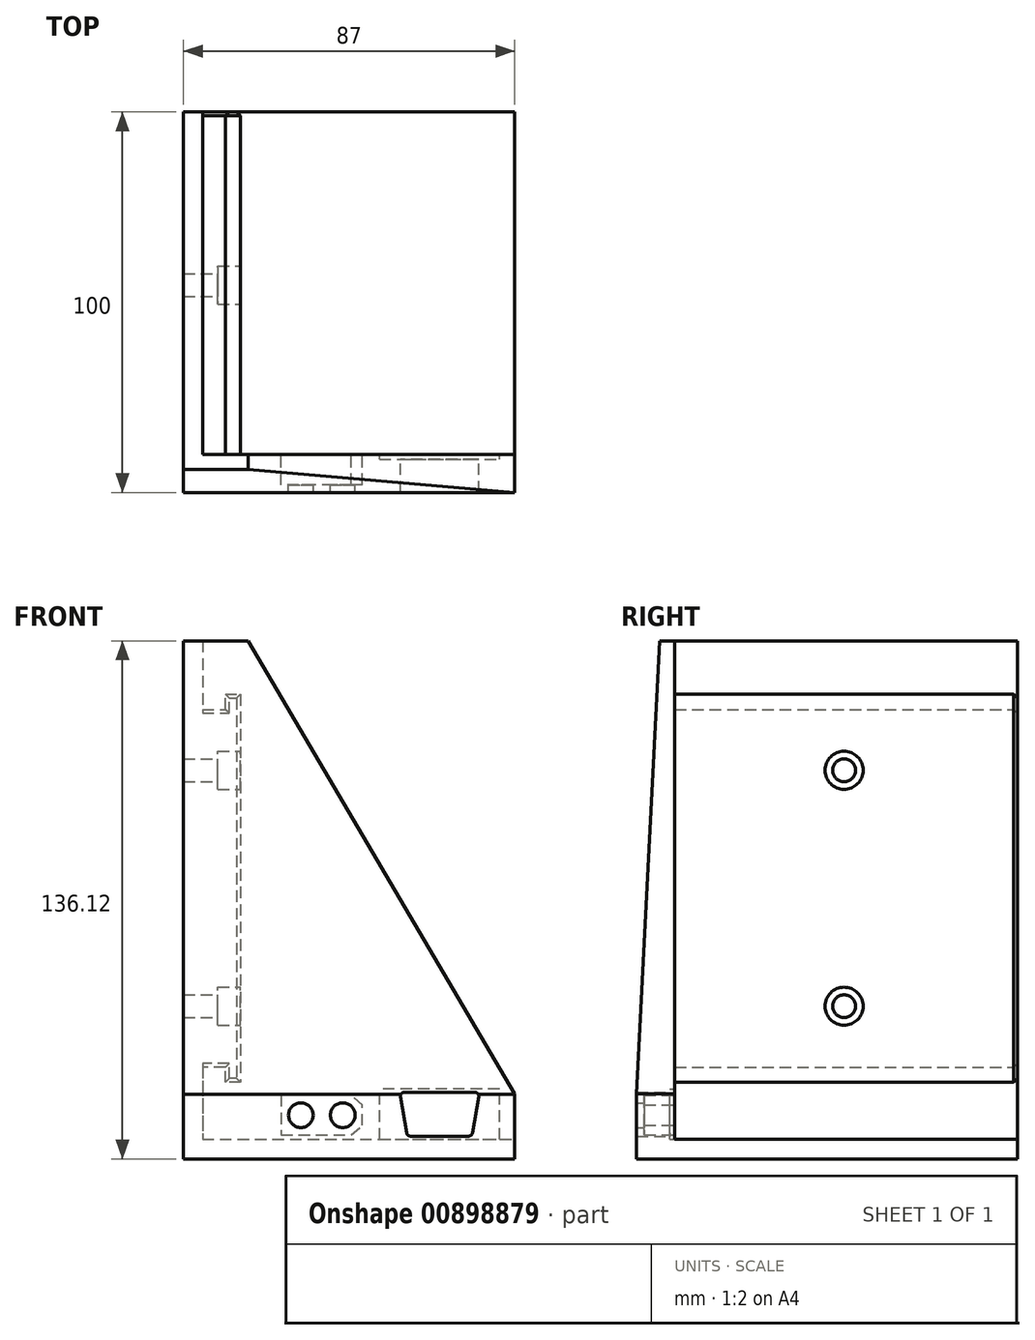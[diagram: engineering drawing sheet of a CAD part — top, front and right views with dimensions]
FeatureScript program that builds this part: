
annotation { "Feature Type Name" : "Feature", "Feature Type Description" : "" }
export const myFeature = defineFeature(function(context is Context, id is Id, definition is map)
    precondition{}
    {
        {
            var Q0;
            Q0=qCreatedBy(makeId("Front.planeOp"),FACE);
            var sketch = newSketch(context, id + "F0", { "sketchPlane" : qUnion([Q0])});
            skLineSegment(sketch, "E0", {"start": v(0, 131) * mm, "end": v(0, 0) * mm});
            skLineSegment(sketch, "E1", {"start": v(0, 131) * mm, "end": v(5, 131) * mm});
            skLineSegment(sketch, "E2", {"start": v(5, 131) * mm, "end": v(5, 113) * mm});
            skLineSegment(sketch, "E3", {"start": v(5, 113) * mm, "end": v(11, 113) * mm});
            skLineSegment(sketch, "E4", {"start": v(11, 113) * mm, "end": v(11, 117) * mm});
            skLineSegment(sketch, "E5", {"start": v(11, 117) * mm, "end": v(15, 117) * mm});
            skLineSegment(sketch, "E6", {"start": v(15, 117) * mm, "end": v(15, 15) * mm});
            skLineSegment(sketch, "E7", {"start": v(15, 15) * mm, "end": v(11, 15) * mm});
            skLineSegment(sketch, "E8", {"start": v(11, 15) * mm, "end": v(11, 19) * mm});
            skLineSegment(sketch, "E9", {"start": v(11, 19) * mm, "end": v(5, 19) * mm});
            skLineSegment(sketch, "E10", {"start": v(5, 19) * mm, "end": v(5, 0) * mm});
            skLineSegment(sketch, "E11", {"start": v(5, 0) * mm, "end": v(0, 0) * mm});
            skLineSegment(sketch, "E12", {"start": v(5, 0) * mm, "end": v(87, 0) * mm});
            skLineSegment(sketch, "E13", {"start": v(87, 0) * mm, "end": v(87, -5.12) * mm});
            skLineSegment(sketch, "E14", {"start": v(87, -5.12) * mm, "end": v(0, -5.12) * mm});
            skLineSegment(sketch, "E15", {"start": v(0, -5.12) * mm, "end": v(0, 0) * mm});
            skSolve(sketch);
        }
        {
            var Q0;
            Q0=qSketchRegion(id+"F0",true);
            extrude(context, id + "F1", {"entities" : qUnion([Q0]), "depth" : 90 * mm, "offsetDistance" : 25 * mm});
        }
        {
            var Q0;
            Q0=makeQuery(id+"F1.opExtrude","CAP_FACE",FACE,{"disambiguationData":[OSD([sQuery(id+"F0.wireOp",EDGE,"E0"),sQuery(id+"F0.wireOp",EDGE,"E1"),sQuery(id+"F0.wireOp",EDGE,"E2"),sQuery(id+"F0.wireOp",EDGE,"E3"),sQuery(id+"F0.wireOp",EDGE,"E4"),sQuery(id+"F0.wireOp",EDGE,"E5"),sQuery(id+"F0.wireOp",EDGE,"E6"),sQuery(id+"F0.wireOp",EDGE,"E7"),sQuery(id+"F0.wireOp",EDGE,"E8"),sQuery(id+"F0.wireOp",EDGE,"E9"),sQuery(id+"F0.wireOp",EDGE,"E10"),sQuery(id+"F0.wireOp",EDGE,"E12"),sQuery(id+"F0.wireOp",EDGE,"E13"),sQuery(id+"F0.wireOp",EDGE,"E14"),sQuery(id+"F0.wireOp",EDGE,"E15")])],"isStart":false});
            var sketch = newSketch(context, id + "F2", { "sketchPlane" : qUnion([Q0])});
            skLineSegment(sketch, "E16", {"start": v(87, 0) * mm, "end": v(87, 12) * mm});
            skLineSegment(sketch, "E17", {"start": v(87, 12) * mm, "end": v(17, 131) * mm});
            skLineSegment(sketch, "E18", {"start": v(17, 131) * mm, "end": v(5, 131) * mm});
            skSolve(sketch);
        }
        {
            var Q0;
            Q0=makeQuery(id+"F2.imprint","IMPRINT",FACE,{"disambiguationData":[TD([[makeQuery(id+"F2.imprint","IMPRINT",EDGE,{"derivedFrom":makeQuery(id+"F1.opExtrude","CAP_EDGE",EDGE,{"disambiguationData":[OSD([sQuery(id+"F0.wireOp",EDGE,"E1")])],"isStart":false})}),-1.0]])]});
            var Q1;
            Q1=makeQuery(id+"F2.imprint","IMPRINT",FACE,{"disambiguationData":[TD([[makeQuery(id+"F2.imprint","IMPRINT",EDGE,{"derivedFrom":sQuery(id+"F2.wireOp",EDGE,"E16")}),1.0]])]});
            extrude(context, id + "F3", {"entities" : qUnion([Q0, Q1]), "operationType" : NewBodyOperationType.ADD, "depth" : 10 * mm, "offsetDistance" : 25 * mm});
        }
        {
            var Q0;
            {var subQ0=sQuery(id+"F0.wireOp",EDGE,"E15");var subQ1=sQuery(id+"F0.wireOp",EDGE,"E0");Q0=makeQuery(id+"F3.boolean.opBoolean","MERGE",FACE,{"derivedFrom":[makeQuery(id+"F1.opExtrude","SWEPT_FACE",FACE,{"disambiguationData":[OSD([subQ1,subQ0])]}),makeQuery(id+"F3.opExtrude","SWEPT_FACE",FACE,{"disambiguationData":[OSD([subQ1,subQ0])]})]});}
            var sketch = newSketch(context, id + "F4", { "sketchPlane" : qUnion([Q0])});
            skLineSegment(sketch, "E19", {"start": v(94, 131) * mm, "end": v(100, 11.88) * mm});
            skSolve(sketch);
        }
        {
            var Q0;
            {var subQ0=sQuery(id+"F4.wireOp",EDGE,"E19");Q0=makeQuery(id+"F4.imprint","IMPRINT",FACE,{"disambiguationData":[TD([[makeQuery(id+"F4.imprint","IMPRINT",EDGE,{"derivedFrom":subQ0}),1.0]])]});}
            extrude(context, id + "F5", {"entities" : qUnion([Q0]), "operationType" : NewBodyOperationType.REMOVE, "oppositeDirection" : true, "depth" : 90 * mm, "offsetDistance" : 25 * mm});
        }
        {
            var Q0;
            Q0=makeQuery(id+"FeWyEREoeEQpgzg_1.opFillet","BLEND_EDGE",EDGE,{"blendedFrom":[makeQuery(id+"F1.opExtrude","CAP_EDGE",EDGE,{"disambiguationData":[OSD([sQuery(id+"F0.wireOp",EDGE,"E0"),sQuery(id+"F0.wireOp",EDGE,"E15")])],"isStart":true}),makeQuery(id+"F1.opExtrude","SWEPT_FACE",FACE,{"disambiguationData":[OSD([sQuery(id+"F0.wireOp",EDGE,"E2")])]})],"blendedInto":[makeQuery(id+"F1.opExtrude","SWEPT_FACE",FACE,{"disambiguationData":[OSD([sQuery(id+"F0.wireOp",EDGE,"E2")])]})]});
            var Q1;
            Q1=makeQuery(id+"F1.opExtrude","CAP_EDGE",EDGE,{"disambiguationData":[OSD([sQuery(id+"F0.wireOp",EDGE,"E3")])],"isStart":true});
            var Q2;
            Q2=makeQuery(id+"F1.opExtrude","CAP_EDGE",EDGE,{"disambiguationData":[OSD([sQuery(id+"F0.wireOp",EDGE,"E4")])],"isStart":true});
            var Q3;
            Q3=makeQuery(id+"F1.opExtrude","CAP_EDGE",EDGE,{"disambiguationData":[OSD([sQuery(id+"F0.wireOp",EDGE,"E5")])],"isStart":true});
            var Q4;
            Q4=makeQuery(id+"F1.opExtrude","CAP_EDGE",EDGE,{"disambiguationData":[OSD([sQuery(id+"F0.wireOp",EDGE,"E6")])],"isStart":true});
            var Q5;
            Q5=makeQuery(id+"F1.opExtrude","CAP_EDGE",EDGE,{"disambiguationData":[OSD([sQuery(id+"F0.wireOp",EDGE,"E7")])],"isStart":true});
            var Q6;
            Q6=makeQuery(id+"F1.opExtrude","CAP_EDGE",EDGE,{"disambiguationData":[OSD([sQuery(id+"F0.wireOp",EDGE,"E8")])],"isStart":true});
            var Q7;
            Q7=makeQuery(id+"F1.opExtrude","CAP_EDGE",EDGE,{"disambiguationData":[OSD([sQuery(id+"F0.wireOp",EDGE,"E9")])],"isStart":true});
            var Q8;
            Q8=makeQuery(id+"FeWyEREoeEQpgzg_1.opFillet","BLEND_EDGE",EDGE,{"blendedFrom":[makeQuery(id+"F1.opExtrude","CAP_EDGE",EDGE,{"disambiguationData":[OSD([sQuery(id+"F0.wireOp",EDGE,"E0"),sQuery(id+"F0.wireOp",EDGE,"E15")])],"isStart":true}),makeQuery(id+"F1.opExtrude","SWEPT_FACE",FACE,{"disambiguationData":[OSD([sQuery(id+"F0.wireOp",EDGE,"E10")])]})],"blendedInto":[makeQuery(id+"F1.opExtrude","SWEPT_FACE",FACE,{"disambiguationData":[OSD([sQuery(id+"F0.wireOp",EDGE,"E10")])]})]});
            chamfer(context, id + "F6", {"entities" : qUnion([Q0, Q1, Q2, Q3, Q4, Q5, Q6, Q7, Q8]), "width" : 1 * mm, "tangentPropagation" : true});
        }
        {
            var Q0;
            Q0=makeQuery(id+"F3.opExtrude","CAP_FACE",FACE,{"disambiguationData":[OSD([sQuery(id+"F0.wireOp",EDGE,"E0"),sQuery(id+"F0.wireOp",EDGE,"E1"),sQuery(id+"F0.wireOp",EDGE,"E13"),sQuery(id+"F0.wireOp",EDGE,"E14"),sQuery(id+"F0.wireOp",EDGE,"E15"),sQuery(id+"F2.wireOp",EDGE,"E16"),sQuery(id+"F2.wireOp",EDGE,"E17"),sQuery(id+"F2.wireOp",EDGE,"E18")])],"isStart":true});
            var sketch = newSketch(context, id + "F7", { "sketchPlane" : qUnion([Q0])});
            skLineSegment(sketch, "E20", {"start": v(-25.63, 11.63) * mm, "end": v(-25.63, 1.13) * mm});
            skLineSegment(sketch, "E21", {"start": v(-25.63, 1.12) * mm, "end": v(-44.03, 1.12) * mm});
            skLineSegment(sketch, "E22", {"start": v(-44.03, 1.13) * mm, "end": v(-47.03, 3.68) * mm});
            skLineSegment(sketch, "E23", {"start": v(-47.03, 3.68) * mm, "end": v(-47.03, 9.08) * mm});
            skLineSegment(sketch, "E24", {"start": v(-47.03, 9.08) * mm, "end": v(-44.03, 11.63) * mm});
            skLineSegment(sketch, "E25", {"start": v(-44.03, 11.62) * mm, "end": v(-25.63, 11.62) * mm});
            skSolve(sketch);
        }
        {
            var Q0;
            Q0=qSketchRegion(id+"F7",true);
            extrude(context, id + "F8", {"entities" : qUnion([Q0]), "operationType" : NewBodyOperationType.REMOVE, "oppositeDirection" : true, "depth" : 8 * mm, "offsetDistance" : 25 * mm});
        }
        {
            var Q0;
            Q0=makeQuery(id+"F8.boolean.opBoolean","COPY",FACE,{"derivedFrom":makeQuery(id+"F8.opExtrude","CAP_FACE",FACE,{"disambiguationData":[OSD([sQuery(id+"F7.wireOp",EDGE,"E20"),sQuery(id+"F7.wireOp",EDGE,"E21"),sQuery(id+"F7.wireOp",EDGE,"E22"),sQuery(id+"F7.wireOp",EDGE,"E23"),sQuery(id+"F7.wireOp",EDGE,"E24"),sQuery(id+"F7.wireOp",EDGE,"E25")])],"isStart":false})});
            var sketch = newSketch(context, id + "F9", { "sketchPlane" : qUnion([Q0])});
            skLineSegment(sketch, "E26", {"start": v(-41.83, 11.62) * mm, "end": v(-41.83, 1.12) * mm, "construction": true});
            skLineSegment(sketch, "E27", {"start": v(-30.83, 11.62) * mm, "end": v(-30.83, 1.12) * mm, "construction": true});
            skCircle(sketch, "E28", {"center": v(-41.83, 6.37) * mm, "radius": 3.25 * mm});
            skCircle(sketch, "E29", {"center": v(-30.83, 6.37) * mm, "radius": 3.25 * mm});
            skSolve(sketch);
        }
        {
            var Q0;
            Q0=qSketchRegion(id+"F9",true);
            extrude(context, id + "F10", {"entities" : qUnion([Q0]), "operationType" : NewBodyOperationType.REMOVE, "oppositeDirection" : true, "depth" : 25 * mm, "offsetDistance" : 25 * mm});
        }
        {
            var Q0;
            Q0=makeQuery(id+"F2.imprint","IMPRINT",FACE,{"disambiguationData":[TD([[makeQuery(id+"F2.imprint","IMPRINT",EDGE,{"derivedFrom":sQuery(id+"F2.wireOp",EDGE,"E16")}),1.0]])]});
            var sketch = newSketch(context, id + "F11", { "sketchPlane" : qUnion([Q0])});
            skLineSegment(sketch, "E30", {"start": v(59.6, 0.85) * mm, "end": v(74.9, 0.85) * mm});
            skLineSegment(sketch, "E31", {"start": v(75.9, 1.68) * mm, "end": v(77.55, 11.18) * mm});
            skLineSegment(sketch, "E32", {"start": v(76.56, 12.35) * mm, "end": v(57.94, 12.35) * mm});
            skLineSegment(sketch, "E33", {"start": v(56.95, 11.18) * mm, "end": v(58.6, 1.68) * mm});
            skPoint(sketch, "E34.visualSharp", {"position": v(56.75, 12.35) * mm});
            skArc(sketch, "E34.filletArc", {"start": v(57.94, 12.35) * mm, "mid": v(57.17, 12) * mm, "end": v(56.95, 11.18) * mm});
            skPoint(sketch, "E35.visualSharp", {"position": v(77.75, 12.35) * mm});
            skArc(sketch, "E35.filletArc", {"start": v(77.55, 11.18) * mm, "mid": v(77.33, 12) * mm, "end": v(76.56, 12.35) * mm});
            skPoint(sketch, "E36.visualSharp", {"position": v(75.75, 0.85) * mm});
            skArc(sketch, "E36.filletArc", {"start": v(74.9, 0.85) * mm, "mid": v(75.55, 1.08) * mm, "end": v(75.9, 1.68) * mm});
            skPoint(sketch, "E37.visualSharp", {"position": v(58.75, 0.85) * mm});
            skArc(sketch, "E37.filletArc", {"start": v(58.6, 1.68) * mm, "mid": v(58.95, 1.08) * mm, "end": v(59.6, 0.85) * mm});
            skLineSegment(sketch, "E38.bottom", {"start": v(83, 0) * mm, "end": v(51.5, 0) * mm});
            skLineSegment(sketch, "E38.top", {"start": v(83, 13.2) * mm, "end": v(51.5, 13.2) * mm});
            skLineSegment(sketch, "E38.left", {"start": v(83, 0) * mm, "end": v(83, 13.2) * mm});
            skLineSegment(sketch, "E38.right", {"start": v(51.5, 0) * mm, "end": v(51.5, 13.2) * mm});
            skSolve(sketch);
        }
        {
            var Q0;
            Q0=makeQuery(id+"F11.imprint","IMPRINT",FACE,{"disambiguationData":[TD([[makeQuery(id+"F11.imprint","IMPRINT",EDGE,{"derivedFrom":sQuery(id+"F11.wireOp",EDGE,"E30")}),1.0]])]});
            extrude(context, id + "F12", {"entities" : qUnion([Q0]), "operationType" : NewBodyOperationType.REMOVE, "depth" : 25 * mm, "offsetDistance" : 25 * mm});
        }
        {
            var Q0;
            Q0=makeQuery(id+"F11.imprint","IMPRINT",FACE,{"disambiguationData":[TD([[makeQuery(id+"F11.imprint","IMPRINT",EDGE,{"derivedFrom":sQuery(id+"F11.wireOp",EDGE,"E30")}),-1.0]])]});
            extrude(context, id + "F13", {"entities" : qUnion([Q0]), "operationType" : NewBodyOperationType.REMOVE, "depth" : 1.25 * mm, "offsetDistance" : 25 * mm});
        }
        {
            var Q0;
            Q0=makeQuery(id+"F1.opExtrude","SWEPT_FACE",FACE,{"disambiguationData":[OSD([sQuery(id+"F0.wireOp",EDGE,"E6")])]});
            var sketch = newSketch(context, id + "F14", { "sketchPlane" : qUnion([Q0])});
            skCircle(sketch, "E39", {"center": v(-45.5, 97) * mm, "radius": 3 * mm});
            skPoint(sketch, "E39.centerSnap0", {"position": v(-45.5, 117) * mm});
            skCircle(sketch, "E40", {"center": v(-45.5, 35) * mm, "radius": 3 * mm});
            skCircle(sketch, "E41", {"center": v(-45.5, 97) * mm, "radius": 5 * mm});
            skCircle(sketch, "E42", {"center": v(-45.5, 35) * mm, "radius": 5 * mm});
            skSolve(sketch);
        }
        {
            var Q0;
            Q0 = qSketchRegion(id + "F14", true);
            extrude(context, id + "F15", {"entities" : qUnion([Q0]), "operationType" : NewBodyOperationType.REMOVE, "oppositeDirection" : true, "depth" : 6 * mm, "offsetDistance" : 25 * mm});
        }
        {
            var Q0;
            Q0=makeQuery(id+"F15.boolean.opBoolean","SPLIT",FACE,{"disambiguationData":[TD([makeQuery(id+"F15.opExtrude","SWEPT_FACE",FACE,{"disambiguationData":[OSD([sQuery(id+"F14.wireOp",EDGE,"E39")])]})])],"derivedFrom":makeQuery(id+"F1.opExtrude","SWEPT_FACE",FACE,{"disambiguationData":[OSD([sQuery(id+"F0.wireOp",EDGE,"E6")])]})});
            var Q1;
            Q1=makeQuery(id+"F15.boolean.opBoolean","SPLIT",FACE,{"disambiguationData":[TD([makeQuery(id+"F15.opExtrude","SWEPT_FACE",FACE,{"disambiguationData":[OSD([sQuery(id+"F14.wireOp",EDGE,"E40")])]})])],"derivedFrom":makeQuery(id+"F1.opExtrude","SWEPT_FACE",FACE,{"disambiguationData":[OSD([sQuery(id+"F0.wireOp",EDGE,"E6")])]})});
            extrude(context, id + "F16", {"entities" : qUnion([Q0, Q1]), "operationType" : NewBodyOperationType.REMOVE, "oppositeDirection" : true, "depth" : 25 * mm, "offsetDistance" : 25 * mm});
        }
    });
